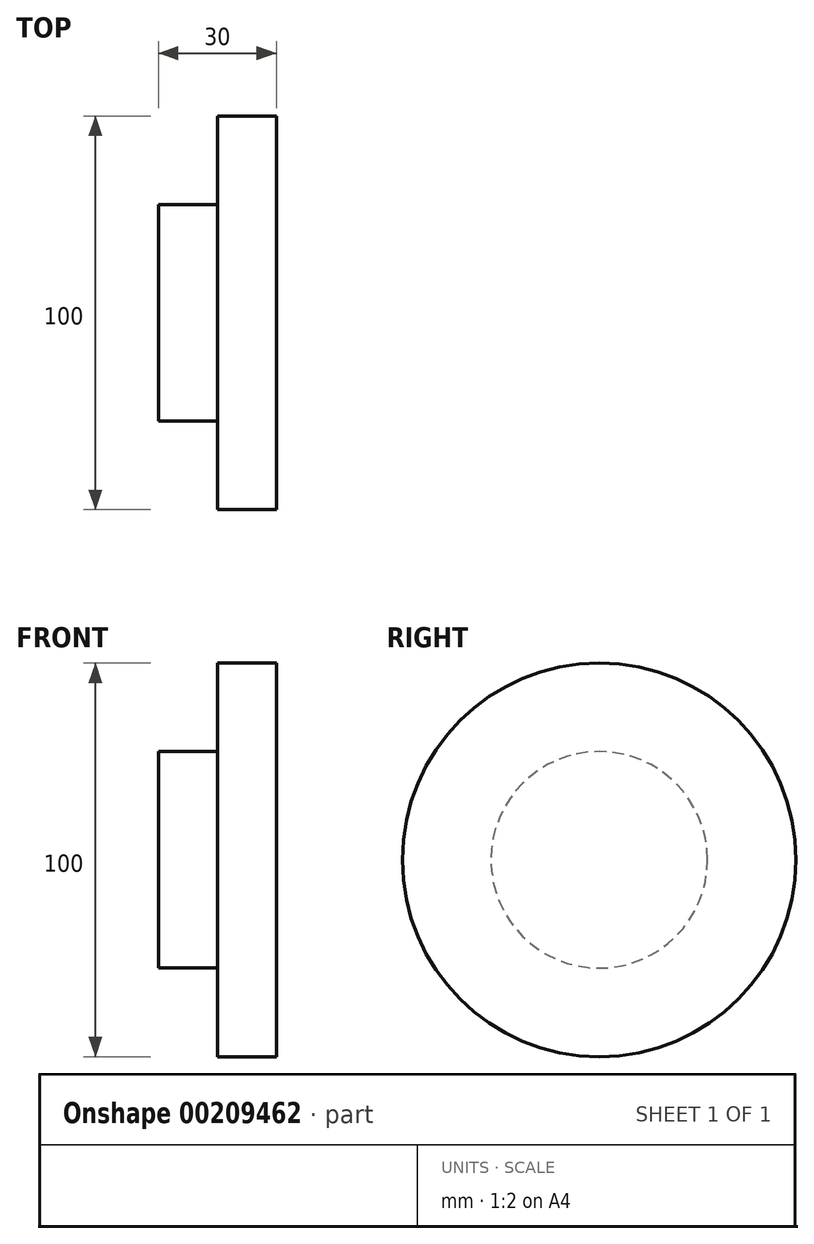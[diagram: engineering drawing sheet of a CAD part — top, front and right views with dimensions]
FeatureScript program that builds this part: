
annotation { "Feature Type Name" : "Feature", "Feature Type Description" : "" }
export const myFeature = defineFeature(function(context is Context, id is Id, definition is map)
    precondition{}
    {
        {
            var Q0;
            Q0=qCreatedBy(makeId("Right.planeOp"),FACE);
            var sketch = newSketch(context, id + "F0", { "sketchPlane" : qUnion([Q0])});
            skCircle(sketch, "E0", {"center": v(0, 0) * mm, "radius": 27.5 * mm});
            skSolve(sketch);
        }
        {
            var Q0;
            Q0=makeQuery(id+"F0.imprint","IMPRINT",FACE,{"disambiguationData":[TD([[makeQuery(id+"F0.imprint","IMPRINT",EDGE,{"derivedFrom":sQuery(id+"F0.wireOp",EDGE,"E0")}),1.0]])]});
            extrude(context, id + "F1", {"entities" : qUnion([Q0]), "depth" : 20 * mm});
        }
        {
            var Q0;
            Q0=makeQuery(id+"F1.opExtrude","CAP_FACE",FACE,{"disambiguationData":[OSD([sQuery(id+"F0.wireOp",EDGE,"E0")])],"isStart":false});
            var sketch = newSketch(context, id + "F2", { "sketchPlane" : qUnion([Q0])});
            skCircle(sketch, "E1", {"center": v(0, 0) * mm, "radius": 50 * mm});
            skSolve(sketch);
        }
        {
            var Q0;
            Q0 = qSketchRegion(id + "F2", true);
            extrude(context, id + "F3", {"entities" : qUnion([Q0]), "operationType" : NewBodyOperationType.ADD, "depth" : 10 * mm, "hasSecondDirection" : true, "secondDirectionOppositeDirection" : true, "secondDirectionDepth" : 5 * mm});
        }
    });
